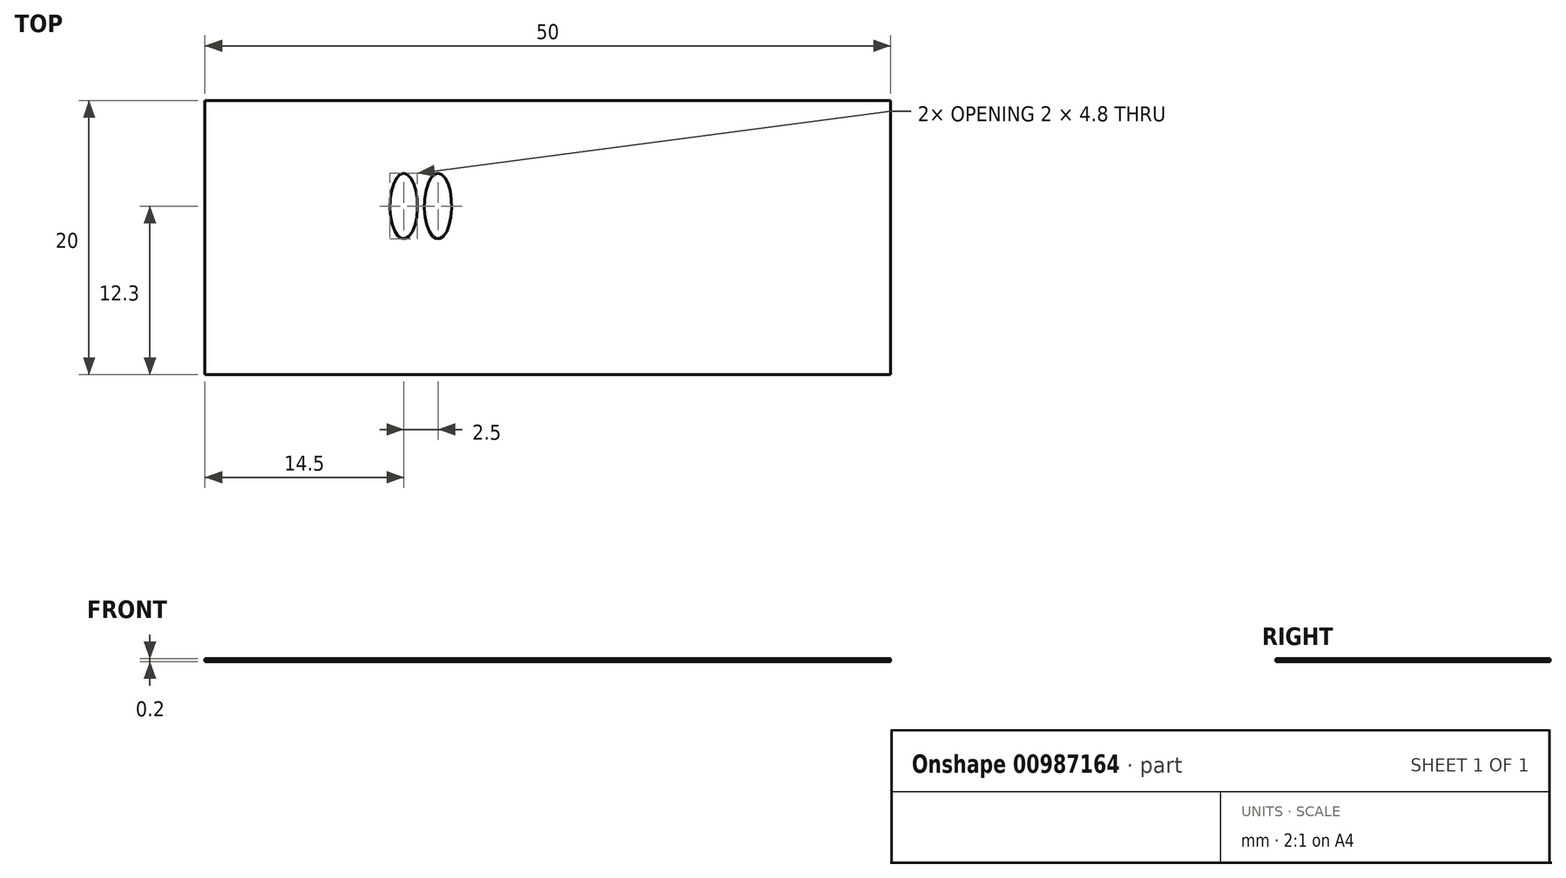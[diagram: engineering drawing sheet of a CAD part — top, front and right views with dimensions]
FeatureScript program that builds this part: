
annotation { "Feature Type Name" : "Feature", "Feature Type Description" : "" }
export const myFeature = defineFeature(function(context is Context, id is Id, definition is map)
    precondition{}
    {
        {
            var Q0;
            Q0=qCreatedBy(makeId("Top.planeOp"),FACE);
            var sketch = newSketch(context, id + "F0", { "sketchPlane" : qUnion([Q0])});
            skLineSegment(sketch, "E0.bottom", {"start": v(0, 0) * mm, "end": v(50, 0) * mm});
            skLineSegment(sketch, "E0.top", {"start": v(0, -20) * mm, "end": v(50, -20) * mm});
            skLineSegment(sketch, "E0.left", {"start": v(0, 0) * mm, "end": v(0, -20) * mm});
            skLineSegment(sketch, "E0.right", {"start": v(50, 0) * mm, "end": v(50, -20) * mm});
            skEllipse(sketch, "E1", {"center": v(14.5, -7.7) * mm, "majorRadius": 1 * mm, "minorRadius": 2.4 * mm, "majorAxis": v(1, 0)});
            skLineSegment(sketch, "E2.direction1", {"start": v(14.5, -7.7) * mm, "end": v(17, -7.7) * mm, "construction": true});
            skEllipse(sketch, "E3.0.1.0", {"center": v(17, -7.7) * mm, "majorRadius": 1 * mm, "minorRadius": 2.4 * mm, "majorAxis": v(1, 0)});
            skLineSegment(sketch, "E4", {"start": v(14.5, -7.7) * mm, "end": v(12.65, -7.7) * mm, "construction": true});
            skLineSegment(sketch, "E5", {"start": v(14.5, -5.3) * mm, "end": v(14.5, -10.1) * mm, "construction": true});
            skSolve(sketch);
        }
        {
            var Q0;
            Q0=makeQuery(id+"F0.imprint","IMPRINT",FACE,{"disambiguationData":[TD([[makeQuery(id+"F0.imprint","IMPRINT",EDGE,{"derivedFrom":sQuery(id+"F0.wireOp",EDGE,"E0.bottom")}),-1.0]])]});
            extrude(context, id + "F1", {"entities" : qUnion([Q0]), "depth" : 0.2 * mm, "offsetDistance" : 25.4 * mm});
        }
    });
